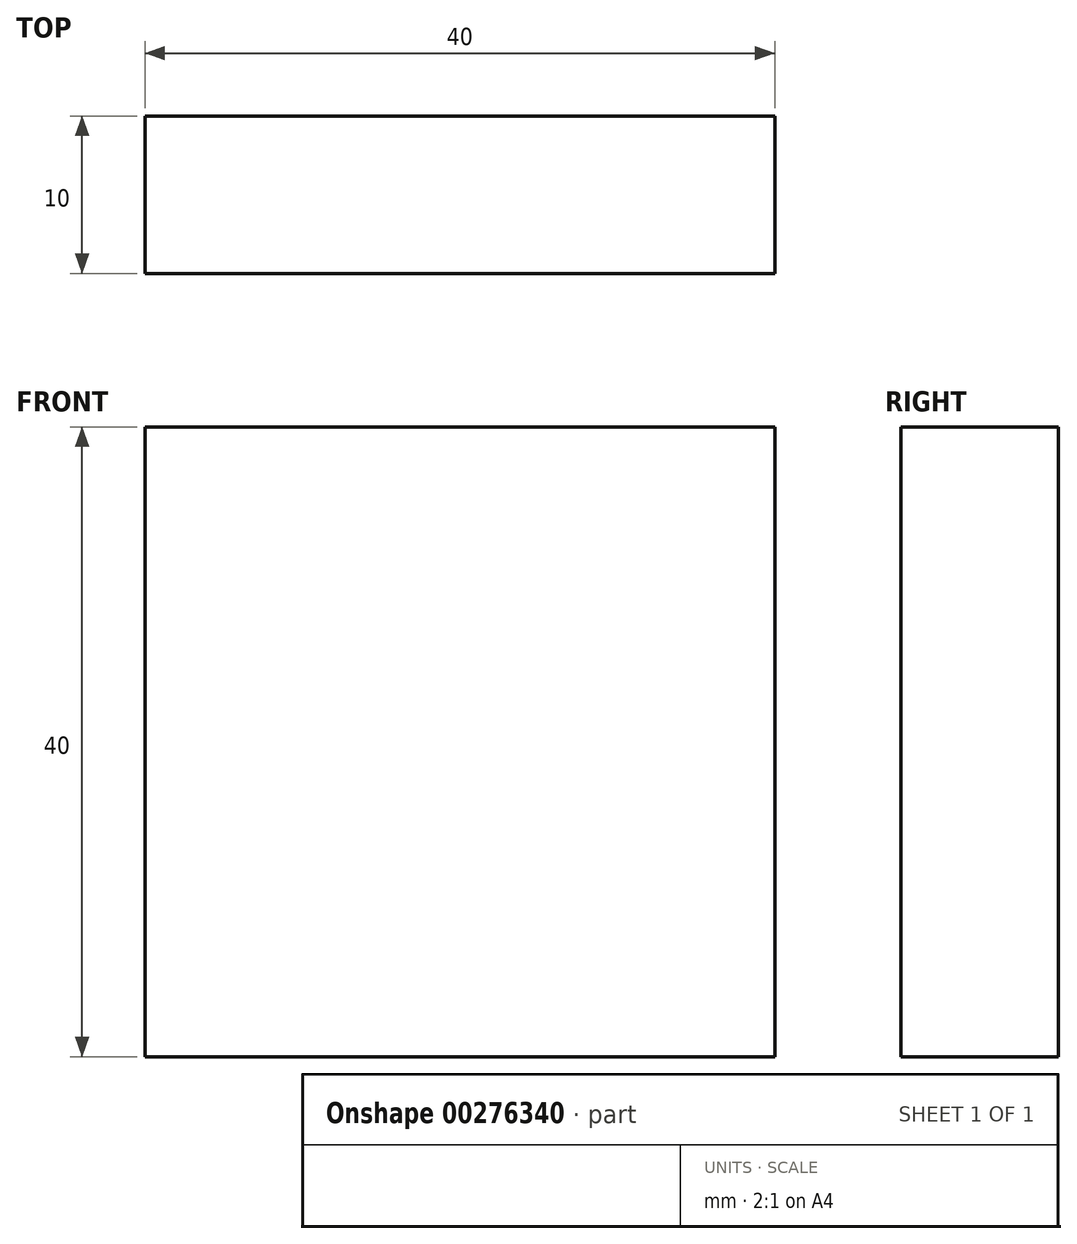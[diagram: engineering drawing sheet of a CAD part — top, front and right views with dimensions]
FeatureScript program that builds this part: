
annotation { "Feature Type Name" : "Feature", "Feature Type Description" : "" }
export const myFeature = defineFeature(function(context is Context, id is Id, definition is map)
    precondition{}
    {
        {
            var Q0;
            Q0=qCreatedBy(makeId("Front.planeOp"),FACE);
            var sketch = newSketch(context, id + "F0", { "sketchPlane" : qUnion([Q0])});
            skLineSegment(sketch, "E0.bottom", {"start": v(-20, 20) * mm, "end": v(20, 20) * mm});
            skLineSegment(sketch, "E0.top", {"start": v(-20, -20) * mm, "end": v(20, -20) * mm});
            skLineSegment(sketch, "E0.left", {"start": v(-20, 20) * mm, "end": v(-20, -20) * mm});
            skLineSegment(sketch, "E0.right", {"start": v(20, 20) * mm, "end": v(20, -20) * mm});
            skPoint(sketch, "E0.middle", {"position": v(0, 0) * mm});
            skSolve(sketch);
        }
        {
            var Q0;
            Q0=makeQuery(id+"F0.imprint","IMPRINT",FACE,{"disambiguationData":[TD([[makeQuery(id+"F0.imprint","IMPRINT",EDGE,{"derivedFrom":sQuery(id+"F0.wireOp",EDGE,"E0.bottom")}),-1.0]])]});
            extrude(context, id + "F1", {"entities" : qUnion([Q0]), "endBound" : BoundingType.SYMMETRIC, "depth" : 10 * mm});
        }
    });
